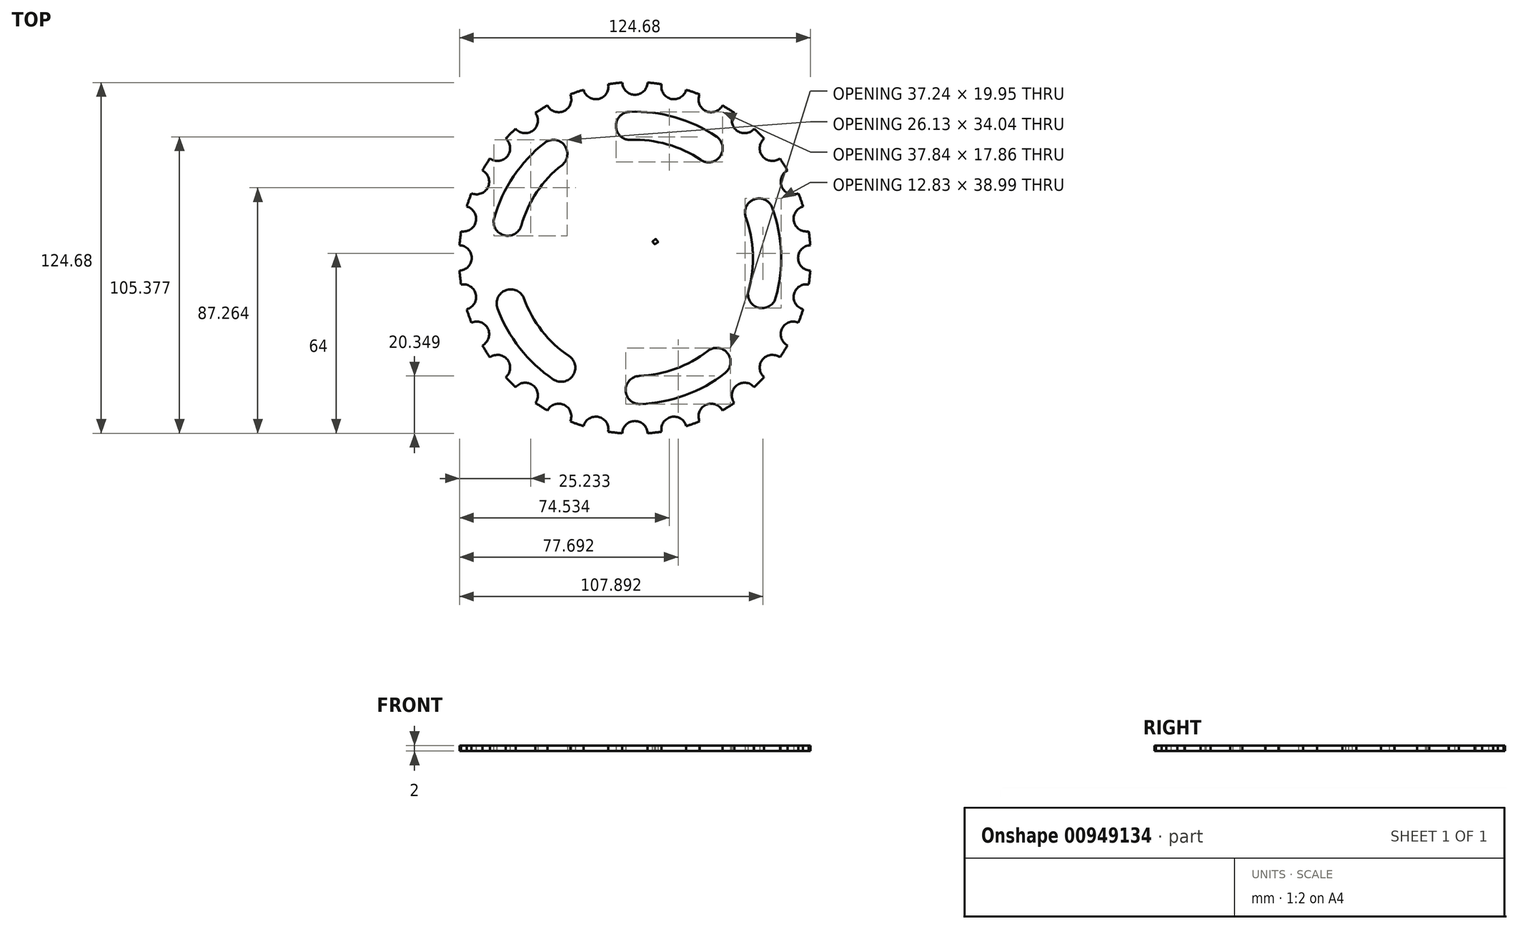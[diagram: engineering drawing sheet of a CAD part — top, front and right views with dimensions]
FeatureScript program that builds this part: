
annotation { "Feature Type Name" : "Feature", "Feature Type Description" : "" }
export const myFeature = defineFeature(function(context is Context, id is Id, definition is map)
    precondition{}
    {
        {
            var Q0;
            Q0=qCreatedBy(makeId("Top.planeOp"),FACE);
            var sketch = newSketch(context, id + "F0", { "sketchPlane" : qUnion([Q0])});
            skCircle(sketch, "E0", {"center": v(0, 0) * mm, "radius": 62.5 * mm});
            skArc(sketch, "E1", {"start": v(-4.5, 62.34) * mm, "mid": v(0, 58) * mm, "end": v(4.5, 62.34) * mm});
            skArc(sketch, "E2.1.0", {"start": v(-18.26, 59.77) * mm, "mid": v(-12.9, 56.54) * mm, "end": v(-9.48, 61.78) * mm});
            skArc(sketch, "E2.2.0", {"start": v(-31.1, 54.21) * mm, "mid": v(-25.16, 52.25) * mm, "end": v(-23, 58.12) * mm});
            skArc(sketch, "E2.3.0", {"start": v(-42.39, 45.93) * mm, "mid": v(-36.16, 45.34) * mm, "end": v(-35.35, 51.54) * mm});
            skArc(sketch, "E2.4.0", {"start": v(-51.54, 35.35) * mm, "mid": v(-45.34, 36.16) * mm, "end": v(-45.93, 42.39) * mm});
            skArc(sketch, "E2.5.0", {"start": v(-58.12, 23) * mm, "mid": v(-52.25, 25.16) * mm, "end": v(-54.21, 31.1) * mm});
            skArc(sketch, "E2.6.0", {"start": v(-61.78, 9.48) * mm, "mid": v(-56.54, 12.9) * mm, "end": v(-59.77, 18.26) * mm});
            skArc(sketch, "E2.7.0", {"start": v(-62.34, -4.5) * mm, "mid": v(-58, 0) * mm, "end": v(-62.34, 4.5) * mm});
            skArc(sketch, "E2.8.0", {"start": v(-59.77, -18.26) * mm, "mid": v(-56.54, -12.9) * mm, "end": v(-61.78, -9.48) * mm});
            skArc(sketch, "E2.9.0", {"start": v(-54.21, -31.1) * mm, "mid": v(-52.25, -25.16) * mm, "end": v(-58.12, -23) * mm});
            skArc(sketch, "E2.10.0", {"start": v(-45.93, -42.39) * mm, "mid": v(-45.34, -36.16) * mm, "end": v(-51.54, -35.35) * mm});
            skArc(sketch, "E2.11.0", {"start": v(-35.35, -51.54) * mm, "mid": v(-36.16, -45.34) * mm, "end": v(-42.39, -45.93) * mm});
            skArc(sketch, "E2.12.0", {"start": v(-23, -58.12) * mm, "mid": v(-25.16, -52.25) * mm, "end": v(-31.1, -54.21) * mm});
            skArc(sketch, "E2.13.0", {"start": v(-9.48, -61.78) * mm, "mid": v(-12.9, -56.54) * mm, "end": v(-18.26, -59.77) * mm});
            skArc(sketch, "E2.14.0", {"start": v(4.5, -62.34) * mm, "mid": v(0, -58) * mm, "end": v(-4.5, -62.34) * mm});
            skArc(sketch, "E2.15.0", {"start": v(18.26, -59.77) * mm, "mid": v(12.9, -56.54) * mm, "end": v(9.48, -61.78) * mm});
            skArc(sketch, "E2.16.0", {"start": v(31.1, -54.21) * mm, "mid": v(25.16, -52.25) * mm, "end": v(23, -58.12) * mm});
            skArc(sketch, "E2.17.0", {"start": v(42.39, -45.93) * mm, "mid": v(36.16, -45.34) * mm, "end": v(35.35, -51.54) * mm});
            skArc(sketch, "E2.18.0", {"start": v(51.54, -35.35) * mm, "mid": v(45.34, -36.16) * mm, "end": v(45.93, -42.39) * mm});
            skArc(sketch, "E2.19.0", {"start": v(58.12, -23) * mm, "mid": v(52.25, -25.16) * mm, "end": v(54.21, -31.1) * mm});
            skArc(sketch, "E2.20.0", {"start": v(61.78, -9.48) * mm, "mid": v(56.54, -12.9) * mm, "end": v(59.77, -18.26) * mm});
            skArc(sketch, "E2.21.0", {"start": v(62.34, 4.5) * mm, "mid": v(58, 0) * mm, "end": v(62.34, -4.5) * mm});
            skArc(sketch, "E2.22.0", {"start": v(59.77, 18.26) * mm, "mid": v(56.54, 12.9) * mm, "end": v(61.78, 9.48) * mm});
            skArc(sketch, "E2.23.0", {"start": v(54.21, 31.1) * mm, "mid": v(52.25, 25.16) * mm, "end": v(58.12, 23) * mm});
            skArc(sketch, "E2.24.0", {"start": v(45.93, 42.39) * mm, "mid": v(45.34, 36.16) * mm, "end": v(51.54, 35.35) * mm});
            skArc(sketch, "E2.25.0", {"start": v(35.35, 51.54) * mm, "mid": v(36.16, 45.34) * mm, "end": v(42.39, 45.93) * mm});
            skArc(sketch, "E2.26.0", {"start": v(23, 58.12) * mm, "mid": v(25.16, 52.25) * mm, "end": v(31.1, 54.21) * mm});
            skArc(sketch, "E2.27.0", {"start": v(9.48, 61.78) * mm, "mid": v(12.9, 56.54) * mm, "end": v(18.26, 59.77) * mm});
            skSolve(sketch);
        }
        {
            var Q0;
            {var subQ8=sQuery(id+"F0.wireOp",EDGE,"E1");Q0=makeQuery(id+"F0.imprint","IMPRINT",FACE,{"disambiguationData":[TD([[makeQuery(id+"F0.imprint","IMPRINT",EDGE,{"derivedFrom":subQ8}),-1.0]])]});}
            extrude(context, id + "F1", {"entities" : qUnion([Q0]), "depth" : 2 * mm, "offsetDistance" : 25 * mm});
        }
        {
            var Q0;
            Q0=qCreatedBy(makeId("Top.planeOp"),FACE);
            var sketch = newSketch(context, id + "F2", { "sketchPlane" : qUnion([Q0])});
            skCircle(sketch, "E3", {"center": v(0, 0) * mm, "radius": 10 * mm});
            skPoint(sketch, "E4.orphan", {"position": v(0, 33.08) * mm});
            skPoint(sketch, "E5", {"position": v(-1.73, 46.97) * mm});
            skPoint(sketch, "E5.positionSnap0", {"position": v(-1.33, 46.97) * mm});
            skArc(sketch, "E6", {"start": v(-1.91, 51.96) * mm, "mid": v(-6.73, 46.78) * mm, "end": v(-1.55, 41.97) * mm});
            skArc(sketch, "E7.1.0", {"start": v(-25.92, 33.05) * mm, "mid": v(-25.07, 40.07) * mm, "end": v(-32.1, 40.92) * mm});
            skArc(sketch, "E7.2.0", {"start": v(-50.01, 14.24) * mm, "mid": v(-46.57, 8.06) * mm, "end": v(-40.4, 11.5) * mm});
            skArc(sketch, "E7.3.0", {"start": v(-39.44, -14.44) * mm, "mid": v(-45.85, -11.46) * mm, "end": v(-48.83, -17.88) * mm});
            skArc(sketch, "E7.4.0", {"start": v(-29, -43.17) * mm, "mid": v(-22.06, -41.8) * mm, "end": v(-23.42, -34.86) * mm});
            skArc(sketch, "E7.5.0", {"start": v(1.55, -41.97) * mm, "mid": v(-3.27, -47.15) * mm, "end": v(1.91, -51.96) * mm});
            skArc(sketch, "E7.6.0", {"start": v(32.1, -40.92) * mm, "mid": v(32.94, -33.9) * mm, "end": v(25.92, -33.05) * mm});
            skArc(sketch, "E7.7.0", {"start": v(40.4, -11.5) * mm, "mid": v(43.83, -17.68) * mm, "end": v(50.01, -14.24) * mm});
            skArc(sketch, "E7.8.0", {"start": v(48.83, 17.88) * mm, "mid": v(42.42, 20.85) * mm, "end": v(39.44, 14.44) * mm});
            skArc(sketch, "E7.9.0", {"start": v(23.42, 34.86) * mm, "mid": v(30.36, 36.23) * mm, "end": v(29, 43.17) * mm});
            skArc(sketch, "E8", {"start": v(-25.92, 33.05) * mm, "mid": v(-34.86, 23.42) * mm, "end": v(-40.4, 11.5) * mm});
            skArc(sketch, "E9", {"start": v(-32.1, 40.92) * mm, "mid": v(-43.17, 29) * mm, "end": v(-50.01, 14.24) * mm});
            skArc(sketch, "E10.trimOffspring", {"start": v(23.42, 34.86) * mm, "mid": v(11.5, 40.4) * mm, "end": v(-1.55, 41.97) * mm});
            skArc(sketch, "E11.trimOffspring", {"start": v(29, 43.17) * mm, "mid": v(14.24, 50.01) * mm, "end": v(-1.91, 51.96) * mm});
            skArc(sketch, "E12.trimOffspring", {"start": v(40.4, -11.5) * mm, "mid": v(41.97, 1.55) * mm, "end": v(39.44, 14.44) * mm});
            skArc(sketch, "E13.trimOffspring", {"start": v(50.01, -14.24) * mm, "mid": v(51.96, 1.91) * mm, "end": v(48.83, 17.88) * mm});
            skArc(sketch, "E14.trimOffspring", {"start": v(1.55, -41.97) * mm, "mid": v(14.44, -39.44) * mm, "end": v(25.92, -33.05) * mm});
            skArc(sketch, "E15.trimOffspring", {"start": v(1.91, -51.96) * mm, "mid": v(17.88, -48.83) * mm, "end": v(32.1, -40.92) * mm});
            skArc(sketch, "E16.trimOffspring", {"start": v(-39.44, -14.44) * mm, "mid": v(-33.05, -25.92) * mm, "end": v(-23.42, -34.86) * mm});
            skArc(sketch, "E17.trimOffspring", {"start": v(-48.83, -17.88) * mm, "mid": v(-40.92, -32.1) * mm, "end": v(-29, -43.17) * mm});
            skSolve(sketch);
        }
        {
            var Q0;
            Q0 = qSketchRegion(id + "F2", true);
            extrude(context, id + "F3", {"entities" : qUnion([Q0]), "operationType" : NewBodyOperationType.REMOVE, "depth" : 2 * mm, "offsetDistance" : 25 * mm});
        }
        {
            var Q0;
            Q0=makeQuery(id+"F1.opExtrude","CAP_FACE",FACE,{"disambiguationData":[OSD([sQuery(id+"F0.wireOp",EDGE,"E0"),sQuery(id+"F0.wireOp",EDGE,"E1"),sQuery(id+"F0.wireOp",EDGE,"E2.1.0"),sQuery(id+"F0.wireOp",EDGE,"E2.2.0"),sQuery(id+"F0.wireOp",EDGE,"E2.3.0"),sQuery(id+"F0.wireOp",EDGE,"E2.4.0"),sQuery(id+"F0.wireOp",EDGE,"E2.5.0"),sQuery(id+"F0.wireOp",EDGE,"E2.6.0"),sQuery(id+"F0.wireOp",EDGE,"E2.7.0"),sQuery(id+"F0.wireOp",EDGE,"E2.8.0"),sQuery(id+"F0.wireOp",EDGE,"E2.9.0"),sQuery(id+"F0.wireOp",EDGE,"E2.10.0"),sQuery(id+"F0.wireOp",EDGE,"E2.11.0"),sQuery(id+"F0.wireOp",EDGE,"E2.12.0"),sQuery(id+"F0.wireOp",EDGE,"E2.13.0"),sQuery(id+"F0.wireOp",EDGE,"E2.14.0"),sQuery(id+"F0.wireOp",EDGE,"E2.15.0"),sQuery(id+"F0.wireOp",EDGE,"E2.16.0"),sQuery(id+"F0.wireOp",EDGE,"E2.17.0"),sQuery(id+"F0.wireOp",EDGE,"E2.18.0"),sQuery(id+"F0.wireOp",EDGE,"E2.19.0"),sQuery(id+"F0.wireOp",EDGE,"E2.20.0"),sQuery(id+"F0.wireOp",EDGE,"E2.21.0"),sQuery(id+"F0.wireOp",EDGE,"E2.22.0"),sQuery(id+"F0.wireOp",EDGE,"E2.23.0"),sQuery(id+"F0.wireOp",EDGE,"E2.24.0"),sQuery(id+"F0.wireOp",EDGE,"E2.25.0"),sQuery(id+"F0.wireOp",EDGE,"E2.26.0"),sQuery(id+"F0.wireOp",EDGE,"E2.27.0")])],"isStart":false});
            var sketch = newSketch(context, id + "F4", { "sketchPlane" : qUnion([Q0])});
            skArc(sketch, "E18", {"start": v(6.25, 5.76) * mm, "mid": v(6.65, 5.3) * mm, "end": v(7, 4.8) * mm});
            skLineSegment(sketch, "E19", {"start": v(6.25, 5.76) * mm, "end": v(7.35, 6.78) * mm});
            skLineSegment(sketch, "E20", {"start": v(7, 4.8) * mm, "end": v(8.25, 5.66) * mm});
            skLineSegment(sketch, "E21.1.0", {"start": v(3.67, 7.67) * mm, "end": v(4.31, 9.02) * mm});
            skArc(sketch, "E21.1.1", {"start": v(2.53, 8.12) * mm, "mid": v(3.1, 7.91) * mm, "end": v(3.67, 7.67) * mm});
            skLineSegment(sketch, "E21.1.2", {"start": v(2.53, 8.12) * mm, "end": v(2.97, 9.55) * mm});
            skLineSegment(sketch, "E21.2.0", {"start": v(-0.66, 8.47) * mm, "end": v(-0.77, 9.97) * mm});
            skArc(sketch, "E21.2.1", {"start": v(-1.87, 8.3) * mm, "mid": v(-1.27, 8.4) * mm, "end": v(-0.66, 8.47) * mm});
            skLineSegment(sketch, "E21.2.2", {"start": v(-1.87, 8.3) * mm, "end": v(-2.2, 9.76) * mm});
            skLineSegment(sketch, "E21.3.0", {"start": v(-4.8, 7) * mm, "end": v(-5.66, 8.25) * mm});
            skArc(sketch, "E21.3.1", {"start": v(-5.76, 6.25) * mm, "mid": v(-5.3, 6.65) * mm, "end": v(-4.8, 7) * mm});
            skLineSegment(sketch, "E21.3.2", {"start": v(-5.76, 6.25) * mm, "end": v(-6.78, 7.35) * mm});
            skLineSegment(sketch, "E21.4.0", {"start": v(-7.67, 3.67) * mm, "end": v(-9.02, 4.31) * mm});
            skArc(sketch, "E21.4.1", {"start": v(-8.12, 2.53) * mm, "mid": v(-7.91, 3.1) * mm, "end": v(-7.67, 3.67) * mm});
            skLineSegment(sketch, "E21.4.2", {"start": v(-8.12, 2.53) * mm, "end": v(-9.55, 2.97) * mm});
            skLineSegment(sketch, "E21.5.0", {"start": v(-8.47, -0.66) * mm, "end": v(-9.97, -0.77) * mm});
            skArc(sketch, "E21.5.1", {"start": v(-8.3, -1.87) * mm, "mid": v(-8.4, -1.27) * mm, "end": v(-8.47, -0.66) * mm});
            skLineSegment(sketch, "E21.5.2", {"start": v(-8.3, -1.87) * mm, "end": v(-9.76, -2.2) * mm});
            skLineSegment(sketch, "E21.6.0", {"start": v(-7, -4.8) * mm, "end": v(-8.25, -5.66) * mm});
            skArc(sketch, "E21.6.1", {"start": v(-6.25, -5.76) * mm, "mid": v(-6.65, -5.3) * mm, "end": v(-7, -4.8) * mm});
            skLineSegment(sketch, "E21.6.2", {"start": v(-6.25, -5.76) * mm, "end": v(-7.35, -6.78) * mm});
            skLineSegment(sketch, "E21.7.0", {"start": v(-3.67, -7.67) * mm, "end": v(-4.31, -9.02) * mm});
            skArc(sketch, "E21.7.1", {"start": v(-2.53, -8.12) * mm, "mid": v(-3.1, -7.91) * mm, "end": v(-3.67, -7.67) * mm});
            skLineSegment(sketch, "E21.7.2", {"start": v(-2.53, -8.12) * mm, "end": v(-2.97, -9.55) * mm});
            skLineSegment(sketch, "E21.8.0", {"start": v(0.66, -8.47) * mm, "end": v(0.77, -9.97) * mm});
            skArc(sketch, "E21.8.1", {"start": v(1.87, -8.3) * mm, "mid": v(1.27, -8.4) * mm, "end": v(0.66, -8.47) * mm});
            skLineSegment(sketch, "E21.8.2", {"start": v(1.87, -8.3) * mm, "end": v(2.2, -9.76) * mm});
            skLineSegment(sketch, "E21.9.0", {"start": v(4.8, -7) * mm, "end": v(5.66, -8.25) * mm});
            skArc(sketch, "E21.9.1", {"start": v(5.76, -6.25) * mm, "mid": v(5.3, -6.65) * mm, "end": v(4.8, -7) * mm});
            skLineSegment(sketch, "E21.9.2", {"start": v(5.76, -6.25) * mm, "end": v(6.78, -7.35) * mm});
            skLineSegment(sketch, "E21.10.0", {"start": v(7.67, -3.67) * mm, "end": v(9.02, -4.31) * mm});
            skArc(sketch, "E21.10.1", {"start": v(8.12, -2.53) * mm, "mid": v(7.91, -3.1) * mm, "end": v(7.67, -3.67) * mm});
            skLineSegment(sketch, "E21.10.2", {"start": v(8.12, -2.53) * mm, "end": v(9.55, -2.97) * mm});
            skLineSegment(sketch, "E21.11.0", {"start": v(8.47, 0.66) * mm, "end": v(9.97, 0.77) * mm});
            skArc(sketch, "E21.11.1", {"start": v(8.3, 1.87) * mm, "mid": v(8.4, 1.27) * mm, "end": v(8.47, 0.66) * mm});
            skLineSegment(sketch, "E21.11.2", {"start": v(8.3, 1.87) * mm, "end": v(9.76, 2.2) * mm});
            skSolve(sketch);
        }
        {
            var Q0;
            {var subQ0=sQuery(id+"F4.wireOp",EDGE,"E21.6.0");Q0=makeQuery(id+"F4.imprint","IMPRINT",FACE,{"disambiguationData":[TD([[makeQuery(id+"F4.imprint","IMPRINT",EDGE,{"derivedFrom":subQ0}),1.0]])]});}
            var Q1;
            {var subQ0=sQuery(id+"F4.wireOp",EDGE,"E21.5.0");Q1=makeQuery(id+"F4.imprint","IMPRINT",FACE,{"disambiguationData":[TD([[makeQuery(id+"F4.imprint","IMPRINT",EDGE,{"derivedFrom":subQ0}),1.0]])]});}
            var Q2;
            {var subQ0=sQuery(id+"F4.wireOp",EDGE,"E21.4.0");Q2=makeQuery(id+"F4.imprint","IMPRINT",FACE,{"disambiguationData":[TD([[makeQuery(id+"F4.imprint","IMPRINT",EDGE,{"derivedFrom":subQ0}),1.0]])]});}
            var Q3;
            {var subQ0=sQuery(id+"F4.wireOp",EDGE,"E21.3.0");Q3=makeQuery(id+"F4.imprint","IMPRINT",FACE,{"disambiguationData":[TD([[makeQuery(id+"F4.imprint","IMPRINT",EDGE,{"derivedFrom":subQ0}),1.0]])]});}
            var Q4;
            {var subQ0=sQuery(id+"F4.wireOp",EDGE,"E21.2.0");Q4=makeQuery(id+"F4.imprint","IMPRINT",FACE,{"disambiguationData":[TD([[makeQuery(id+"F4.imprint","IMPRINT",EDGE,{"derivedFrom":subQ0}),1.0]])]});}
            var Q5;
            {var subQ0=sQuery(id+"F4.wireOp",EDGE,"E21.1.0");Q5=makeQuery(id+"F4.imprint","IMPRINT",FACE,{"disambiguationData":[TD([[makeQuery(id+"F4.imprint","IMPRINT",EDGE,{"derivedFrom":subQ0}),1.0]])]});}
            var Q6;
            Q6=makeQuery(id+"F4.imprint","IMPRINT",FACE,{"disambiguationData":[TD([[makeQuery(id+"F4.imprint","IMPRINT",EDGE,{"derivedFrom":sQuery(id+"F4.wireOp",EDGE,"E18")}),1.0]])]});
            var Q7;
            {var subQ0=sQuery(id+"F4.wireOp",EDGE,"E21.11.0");Q7=makeQuery(id+"F4.imprint","IMPRINT",FACE,{"disambiguationData":[TD([[makeQuery(id+"F4.imprint","IMPRINT",EDGE,{"derivedFrom":subQ0}),1.0]])]});}
            var Q8;
            {var subQ0=sQuery(id+"F4.wireOp",EDGE,"E21.10.0");Q8=makeQuery(id+"F4.imprint","IMPRINT",FACE,{"disambiguationData":[TD([[makeQuery(id+"F4.imprint","IMPRINT",EDGE,{"derivedFrom":subQ0}),1.0]])]});}
            var Q9;
            {var subQ0=sQuery(id+"F4.wireOp",EDGE,"E21.9.0");Q9=makeQuery(id+"F4.imprint","IMPRINT",FACE,{"disambiguationData":[TD([[makeQuery(id+"F4.imprint","IMPRINT",EDGE,{"derivedFrom":subQ0}),1.0]])]});}
            var Q10;
            {var subQ0=sQuery(id+"F4.wireOp",EDGE,"E21.8.0");Q10=makeQuery(id+"F4.imprint","IMPRINT",FACE,{"disambiguationData":[TD([[makeQuery(id+"F4.imprint","IMPRINT",EDGE,{"derivedFrom":subQ0}),1.0]])]});}
            var Q11;
            {var subQ0=sQuery(id+"F4.wireOp",EDGE,"E21.7.0");Q11=makeQuery(id+"F4.imprint","IMPRINT",FACE,{"disambiguationData":[TD([[makeQuery(id+"F4.imprint","IMPRINT",EDGE,{"derivedFrom":subQ0}),1.0]])]});}
            extrude(context, id + "F5", {"entities" : qUnion([Q0, Q1, Q2, Q3, Q4, Q5, Q6, Q7, Q8, Q9, Q10, Q11]), "operationType" : NewBodyOperationType.ADD, "oppositeDirection" : true, "depth" : 2 * mm, "offsetDistance" : 25 * mm});
        }
    });
